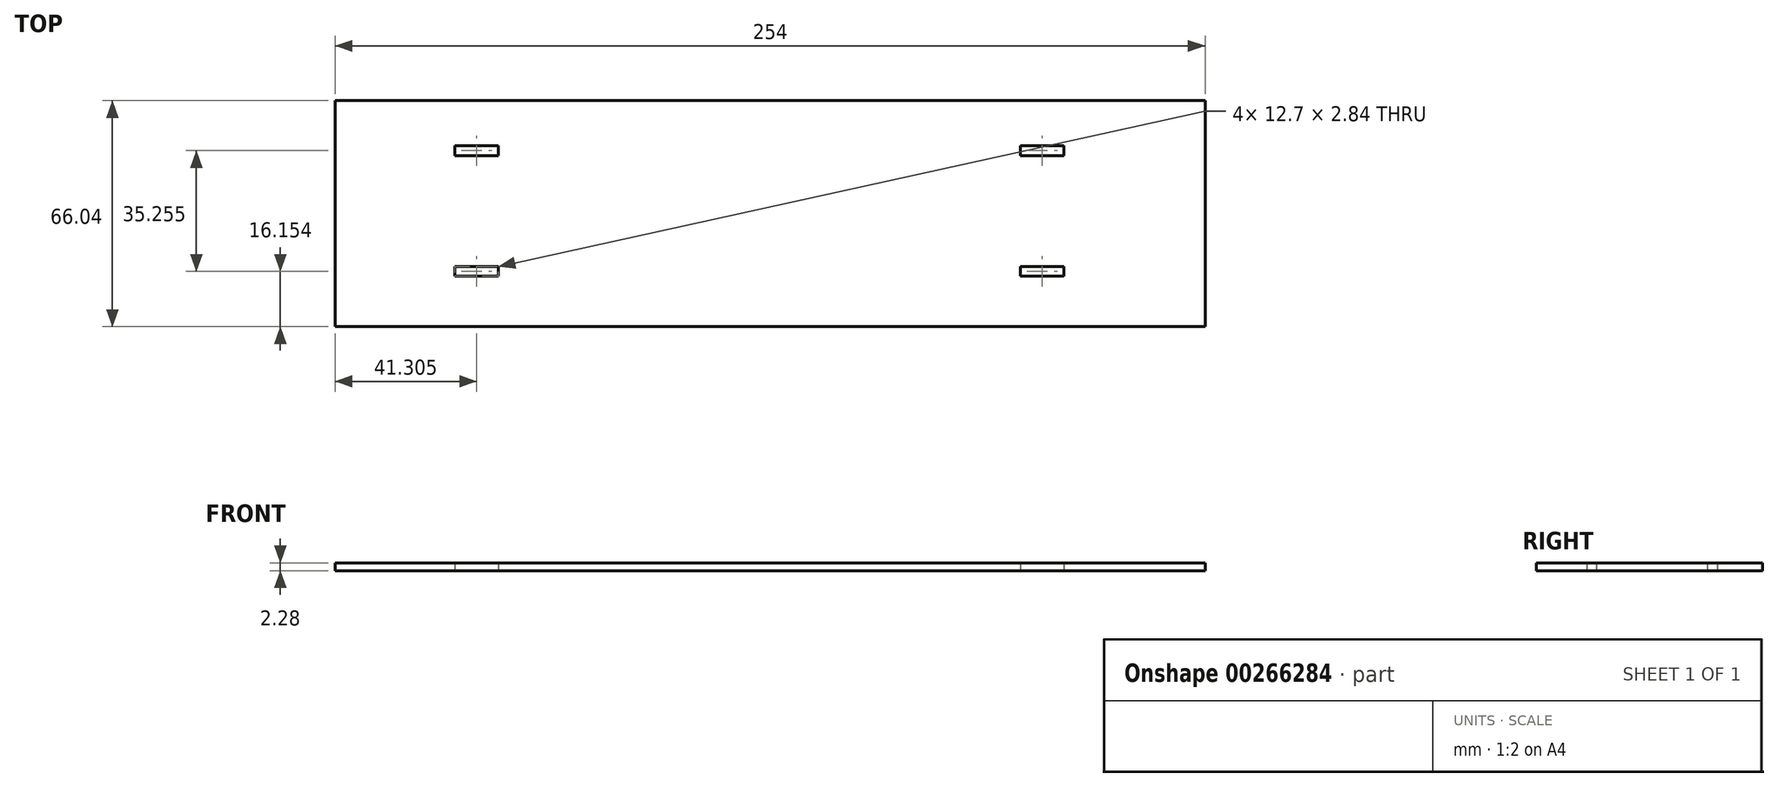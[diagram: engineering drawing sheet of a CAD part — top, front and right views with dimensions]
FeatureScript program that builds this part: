
annotation { "Feature Type Name" : "Feature", "Feature Type Description" : "" }
export const myFeature = defineFeature(function(context is Context, id is Id, definition is map)
    precondition{}
    {
        {
            var Q0;
            Q0=qCreatedBy(makeId("Top.planeOp"),FACE);
            var sketch = newSketch(context, id + "F0", { "sketchPlane" : qUnion([Q0])});
            skLineSegment(sketch, "E0.bottom", {"start": v(127, 33.02) * mm, "end": v(-127, 33.02) * mm});
            skLineSegment(sketch, "E0.top", {"start": v(127, -33.02) * mm, "end": v(-127, -33.02) * mm});
            skLineSegment(sketch, "E0.left", {"start": v(127, 33.02) * mm, "end": v(127, -33.02) * mm});
            skLineSegment(sketch, "E0.right", {"start": v(-127, 33.02) * mm, "end": v(-127, -33.02) * mm});
            skPoint(sketch, "E0.middle", {"position": v(0, 0) * mm});
            skLineSegment(sketch, "E1.bottom", {"start": v(-79.34, -15.44) * mm, "end": v(-92.04, -15.44) * mm});
            skLineSegment(sketch, "E1.top", {"start": v(-79.34, -18.29) * mm, "end": v(-92.04, -18.29) * mm});
            skLineSegment(sketch, "E1.left", {"start": v(-79.34, -15.44) * mm, "end": v(-79.34, -18.29) * mm});
            skLineSegment(sketch, "E1.right", {"start": v(-92.04, -15.44) * mm, "end": v(-92.04, -18.29) * mm});
            skPoint(sketch, "E1.middle", {"position": v(-85.7, -16.87) * mm});
            skLineSegment(sketch, "E2.bottom", {"start": v(85.76, -18.29) * mm, "end": v(73.06, -18.29) * mm});
            skLineSegment(sketch, "E2.top", {"start": v(85.76, -15.44) * mm, "end": v(73.06, -15.44) * mm});
            skLineSegment(sketch, "E2.left", {"start": v(85.76, -18.29) * mm, "end": v(85.76, -15.44) * mm});
            skLineSegment(sketch, "E2.right", {"start": v(73.06, -18.29) * mm, "end": v(73.06, -15.44) * mm});
            skPoint(sketch, "E2.middle", {"position": v(79.4, -16.87) * mm});
            skLineSegment(sketch, "E3.bottom", {"start": v(-79.34, 19.81) * mm, "end": v(-92.04, 19.81) * mm});
            skLineSegment(sketch, "E3.top", {"start": v(-79.34, 16.97) * mm, "end": v(-92.04, 16.97) * mm});
            skLineSegment(sketch, "E3.left", {"start": v(-79.34, 19.81) * mm, "end": v(-79.34, 16.97) * mm});
            skLineSegment(sketch, "E3.right", {"start": v(-92.04, 19.81) * mm, "end": v(-92.04, 16.97) * mm});
            skPoint(sketch, "E3.middle", {"position": v(-85.7, 18.39) * mm});
            skPoint(sketch, "E3.middle.positionSnap0", {"position": v(-85.7, -15.44) * mm});
            skPoint(sketch, "E3.centerSnap0", {"position": v(-85.7, -15.44) * mm});
            skLineSegment(sketch, "E4.bottom", {"start": v(73.06, 16.97) * mm, "end": v(85.76, 16.97) * mm});
            skLineSegment(sketch, "E4.top", {"start": v(73.06, 19.81) * mm, "end": v(85.76, 19.81) * mm});
            skLineSegment(sketch, "E4.left", {"start": v(73.06, 16.97) * mm, "end": v(73.06, 19.81) * mm});
            skLineSegment(sketch, "E4.right", {"start": v(85.76, 16.97) * mm, "end": v(85.76, 19.81) * mm});
            skSolve(sketch);
        }
        {
            var Q0;
            Q0=makeQuery(id+"F0.imprint","IMPRINT",FACE,{"disambiguationData":[TD([[makeQuery(id+"F0.imprint","IMPRINT",EDGE,{"derivedFrom":sQuery(id+"F0.wireOp",EDGE,"E0.bottom")}),1.0]])]});
            extrude(context, id + "F1", {"entities" : qUnion([Q0]), "endBound" : BoundingType.SYMMETRIC, "depth" : 2.3 * mm});
        }
    });
